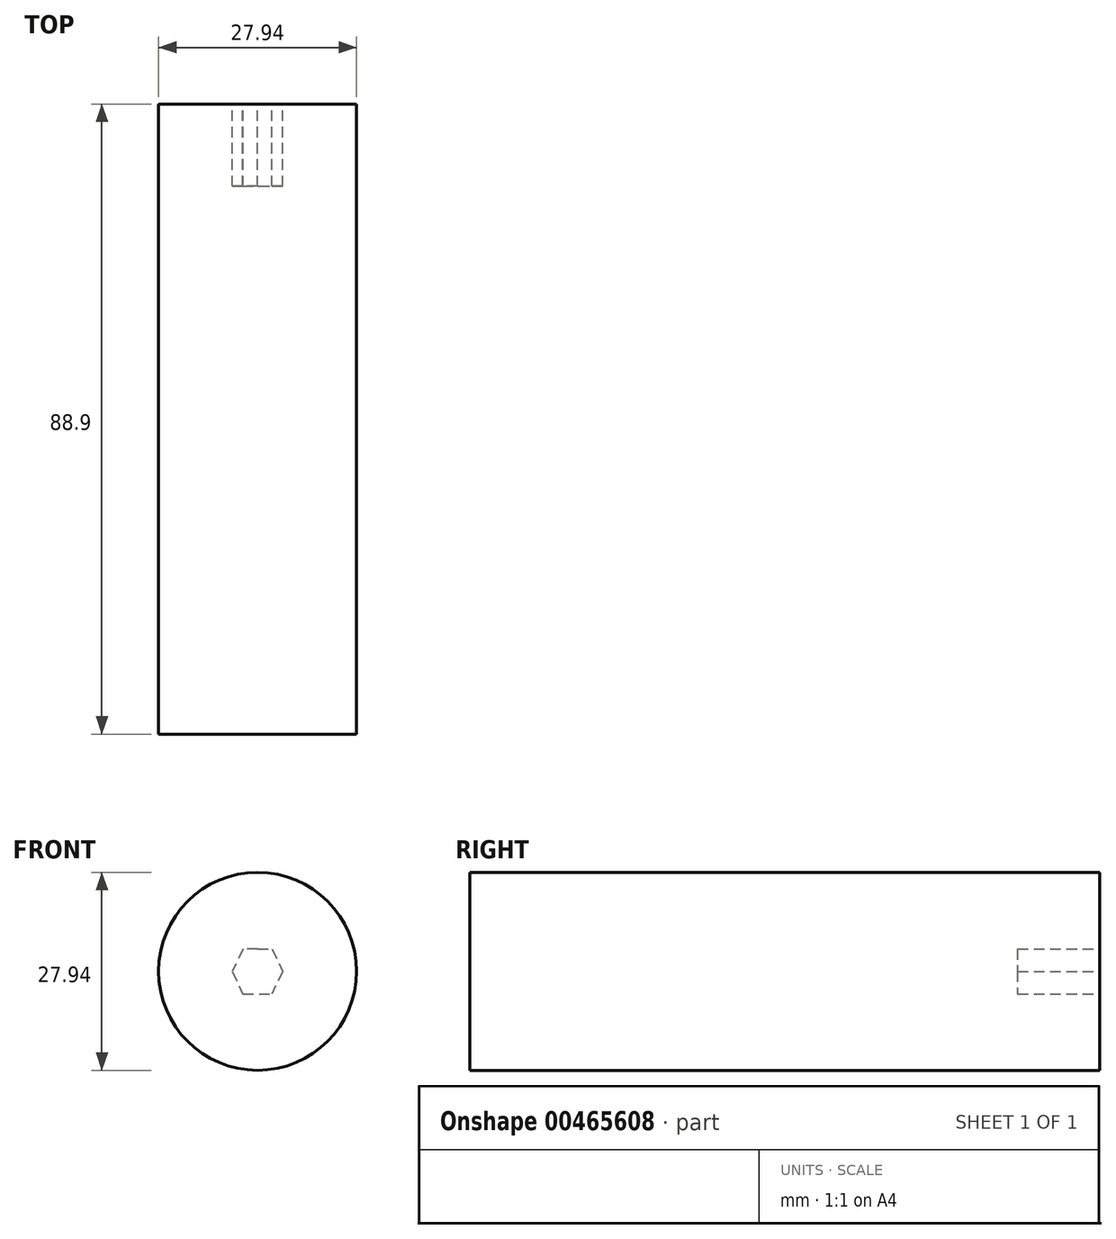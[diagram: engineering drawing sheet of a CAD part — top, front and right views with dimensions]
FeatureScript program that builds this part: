
annotation { "Feature Type Name" : "Feature", "Feature Type Description" : "" }
export const myFeature = defineFeature(function(context is Context, id is Id, definition is map)
    precondition{}
    {
        {
            var Q0;
            Q0=qCreatedBy(makeId("Front.planeOp"),FACE);
            var sketch = newSketch(context, id + "F0", { "sketchPlane" : qUnion([Q0])});
            skCircle(sketch, "E0", {"center": v(0, 0) * mm, "radius": 13.97 * mm});
            skSolve(sketch);
        }
        {
            var Q0;
            Q0=makeQuery(id+"F0.imprint","IMPRINT",FACE,{"disambiguationData":[TD([[makeQuery(id+"F0.imprint","IMPRINT",EDGE,{"derivedFrom":sQuery(id+"F0.wireOp",EDGE,"E0")}),1.0]])]});
            extrude(context, id + "F1", {"entities" : qUnion([Q0]), "depth" : 44.45 * mm});
        }
        {
            var Q0;
            Q0=makeQuery(id+"F1.opExtrude","SWEPT_BODY",BODY,{"disambiguationData":[OSD([sQuery(id+"F0.wireOp",EDGE,"E0")])]});
            var Q1;
            Q1=qCreatedBy(makeId("Front.planeOp"),FACE);
            mirror(context, id + "F2", {"operationType" : NewBodyOperationType.ADD, "entities" : qUnion([Q0]), "mirrorPlane" : qUnion([Q1])});
        }
        {
            var Q0;
            Q0=makeQuery(id+"F2.opPattern","COPY",FACE,{"derivedFrom":makeQuery(id+"F1.opExtrude","CAP_FACE",FACE,{"disambiguationData":[OSD([sQuery(id+"F0.wireOp",EDGE,"E0")])],"isStart":false}),"instanceName":"1"});
            var sketch = newSketch(context, id + "F3", { "sketchPlane" : qUnion([Q0])});
            skLineSegment(sketch, "E1", {"start": v(0, 3.18) * mm, "end": v(2.04, 3.15) * mm});
            skLineSegment(sketch, "E2", {"start": v(0, 3.18) * mm, "end": v(-2.04, 3.18) * mm});
            skLineSegment(sketch, "E3", {"start": v(0.04, -3.18) * mm, "end": v(-2, -3.18) * mm});
            skPoint(sketch, "E4.endSnap0", {"position": v(-0.99, -3.18) * mm});
            skLineSegment(sketch, "E5", {"start": v(2.08, -3.18) * mm, "end": v(0.04, -3.18) * mm});
            skLineSegment(sketch, "E6", {"start": v(2.04, 3.15) * mm, "end": v(3.56, 0) * mm});
            skLineSegment(sketch, "E7", {"start": v(3.56, 0) * mm, "end": v(2.08, -3.18) * mm});
            skLineSegment(sketch, "E8", {"start": v(-3.56, 0) * mm, "end": v(-2, -3.18) * mm});
            skLineSegment(sketch, "E9", {"start": v(-2.04, 3.18) * mm, "end": v(-3.56, 0) * mm});
            skSolve(sketch);
        }
        {
            var Q0;
            Q0 = qSketchRegion(id + "F3", true);
            extrude(context, id + "F4", {"entities" : qUnion([Q0]), "operationType" : NewBodyOperationType.REMOVE, "oppositeDirection" : true, "depth" : 11.6 * mm});
        }
    });
